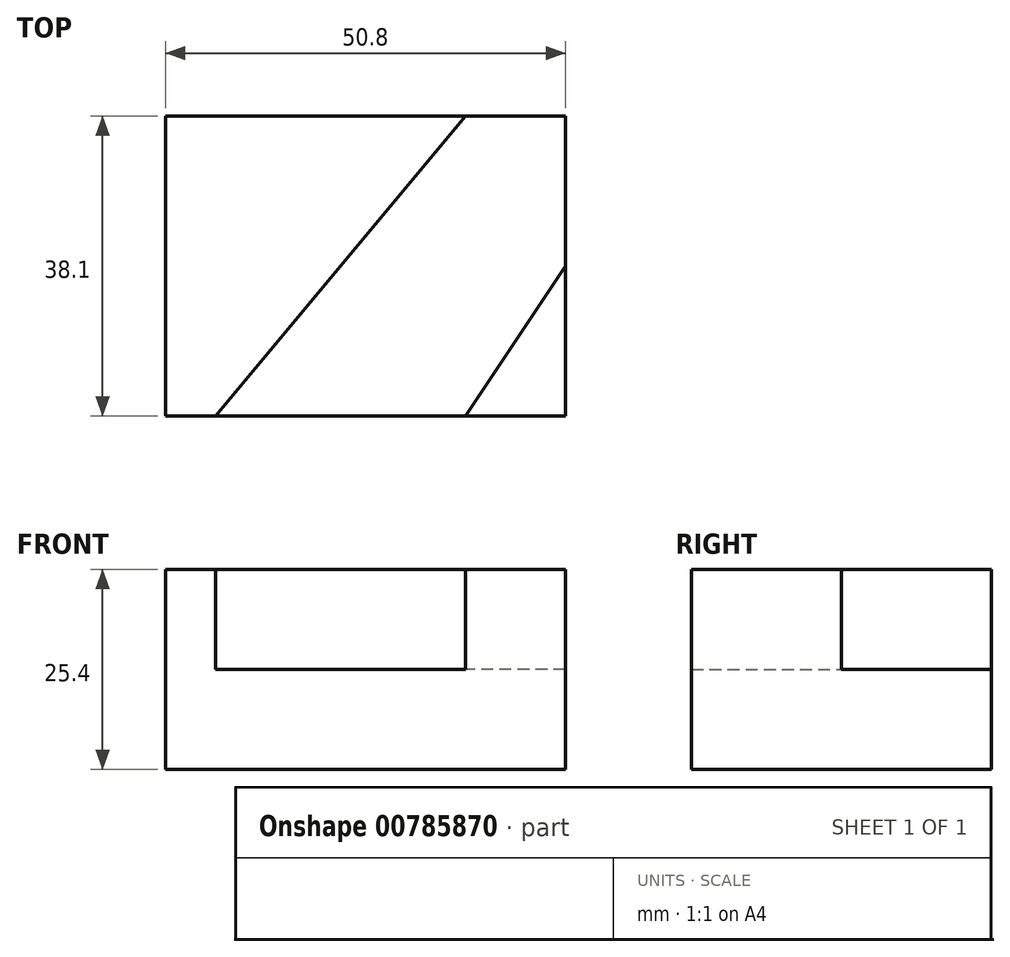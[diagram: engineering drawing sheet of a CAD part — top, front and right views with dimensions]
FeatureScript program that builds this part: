
annotation { "Feature Type Name" : "Feature", "Feature Type Description" : "" }
export const myFeature = defineFeature(function(context is Context, id is Id, definition is map)
    precondition{}
    {
        {
            var Q0;
            Q0=qCreatedBy(makeId("Front.planeOp"),FACE);
            var sketch = newSketch(context, id + "F0", { "sketchPlane" : qUnion([Q0])});
            skLineSegment(sketch, "E0", {"start": v(0, 0) * mm, "end": v(50.8, 0) * mm});
            skLineSegment(sketch, "E1", {"start": v(50.8, 0) * mm, "end": v(50.8, 25.4) * mm});
            skLineSegment(sketch, "E2", {"start": v(50.8, 25.4) * mm, "end": v(0, 25.4) * mm});
            skLineSegment(sketch, "E3", {"start": v(0, 25.4) * mm, "end": v(0, 0) * mm});
            skSolve(sketch);
        }
        {
            var Q0;
            Q0 = qSketchRegion(id + "F0", true);
            extrude(context, id + "F1", {"entities" : qUnion([Q0]), "depth" : 38.1 * mm, "offsetDistance" : 25.4 * mm});
        }
        {
            var Q0;
            Q0=makeQuery(id+"F1.opExtrude","SWEPT_FACE",FACE,{"disambiguationData":[OSD([sQuery(id+"F0.wireOp",EDGE,"E2")])]});
            var sketch = newSketch(context, id + "F2", { "sketchPlane" : qUnion([Q0])});
            skLineSegment(sketch, "E4", {"start": v(0, -38.1) * mm, "end": v(6.35, -38.1) * mm});
            skSolve(sketch);
        }
        {
            var Q0;
            Q0=makeQuery(id+"F1.opExtrude","SWEPT_FACE",FACE,{"disambiguationData":[OSD([sQuery(id+"F0.wireOp",EDGE,"E2")])]});
            var sketch = newSketch(context, id + "F3", { "sketchPlane" : qUnion([Q0])});
            skLineSegment(sketch, "E5", {"start": v(0, 0) * mm, "end": v(38.1, 0) * mm});
            skLineSegment(sketch, "E6", {"start": v(0, -38.1) * mm, "end": v(6.35, -38.1) * mm});
            skLineSegment(sketch, "E7", {"start": v(6.35, -38.1) * mm, "end": v(38.1, 0) * mm});
            skLineSegment(sketch, "E8", {"start": v(0, 0) * mm, "end": v(0, -38.1) * mm});
            skLineSegment(sketch, "E9", {"start": v(50.8, -38.1) * mm, "end": v(38.1, -38.1) * mm});
            skLineSegment(sketch, "E10", {"start": v(38.1, -38.1) * mm, "end": v(50.8, -19.05) * mm});
            skLineSegment(sketch, "E11", {"start": v(50.8, -19.05) * mm, "end": v(50.8, -38.1) * mm});
            skLineSegment(sketch, "E12", {"start": v(38.1, 0) * mm, "end": v(0, 0) * mm});
            skSolve(sketch);
        }
        {
            var Q0;
            {var subQ5=sQuery(id+"F3.wireOp",EDGE,"E7");Q0=makeQuery(id+"F3.imprint","IMPRINT",FACE,{"disambiguationData":[TD([[makeQuery(id+"F3.imprint","IMPRINT",EDGE,{"derivedFrom":subQ5}),-1.0]])]});}
            extrude(context, id + "F4", {"entities" : qUnion([Q0]), "operationType" : NewBodyOperationType.REMOVE, "oppositeDirection" : true, "depth" : 12.7 * mm, "offsetDistance" : 25.4 * mm});
        }
    });
